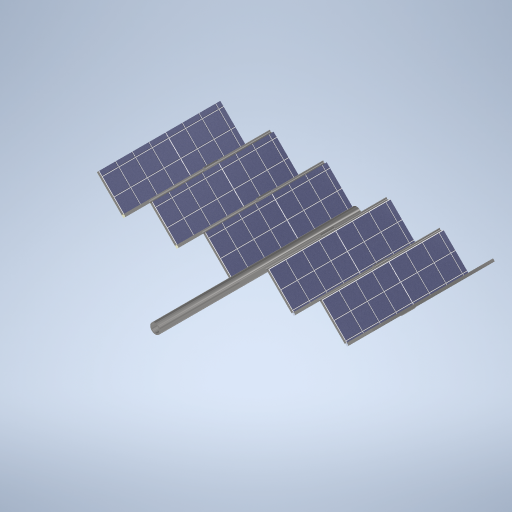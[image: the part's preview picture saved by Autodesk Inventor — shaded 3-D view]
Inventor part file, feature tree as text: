
AUTODESK INVENTOR PART (.ipt)
format: ipt  version: 2024 (Build 280153000, 153)  size: 497,152 bytes
history: native  units: mm
features: other x12, extrude x4, plane x3, mirror x1, loft x1
ambient origin geometry x8: Origin, YZ Plane, XZ Plane, XY Plane, X Axis, Y Axis, Z Axis, Center Point
bodies: Solid1 (feature_tree)
feature tree (21):
  other  "pole_diameter_sketch"
  extrude  "pole_extrude"  Depth=23.1mm
  other  "pole_slot_diameter_sketch"
  extrude  "pole_slot_extrude"  Depth=460.0mm TaperAngle=0.0deg
  plane  "Work Plane1"
  plane  "Work Plane2"
  other  "solar_panel_loft_guide_rear"
  other  "solar_panel_loft_guide_front"
  other  "solar_panel_thickness"
  plane  "Work Plane3"
  other  "solar_panel_hinge_cutout_sketch"
  extrude  "solar_panel_hinge_cutout_extrude"  Depth=17.3mm
  other  "solar_panel_hinge_sketch"
  extrude  "solar_panel_hinge_extrude"  Depth=91.0mm TaperAngle=0.0deg
  mirror  "solar_panel_mirror"
  other  "Srf2"
  other  "Srf4"
  other  "solar_panel_surface_loft"
  loft  "LoftSrf4"
  other  "Finish1"
  other  "Finish2"
